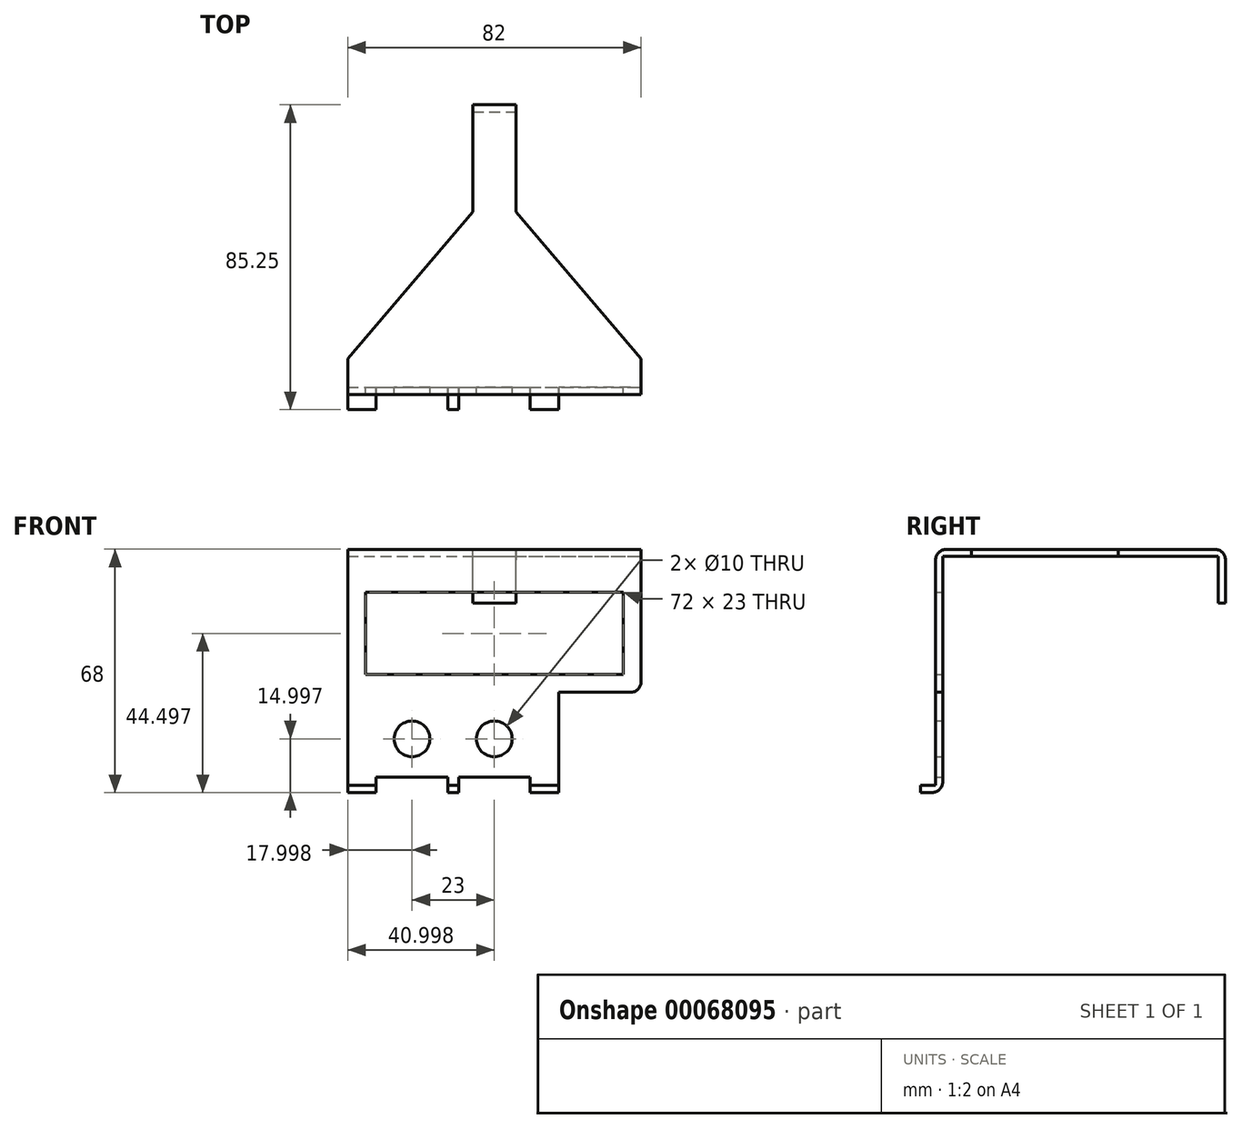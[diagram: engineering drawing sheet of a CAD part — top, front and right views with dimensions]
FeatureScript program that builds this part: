
annotation { "Feature Type Name" : "Feature", "Feature Type Description" : "" }
export const myFeature = defineFeature(function(context is Context, id is Id, definition is map)
    precondition{}
    {
        {
            var Q0;
            Q0=qCreatedBy(makeId("Front.planeOp"),FACE);
            var sketch = newSketch(context, id + "F0", { "sketchPlane" : qUnion([Q0])});
            skLineSegment(sketch, "E0.bottom", {"start": v(-52.13, 38.36) * mm, "end": v(29.87, 38.36) * mm});
            skLineSegment(sketch, "E0.top", {"start": v(-52.13, -29.64) * mm, "end": v(-44.13, -29.64) * mm});
            skLineSegment(sketch, "E0.left", {"start": v(-52.13, 38.36) * mm, "end": v(-52.13, -29.64) * mm});
            skLineSegment(sketch, "E0.right", {"start": v(29.87, 38.36) * mm, "end": v(29.87, 1.36) * mm});
            skLineSegment(sketch, "E1.bottom", {"start": v(-47.13, 26.36) * mm, "end": v(24.87, 26.36) * mm});
            skLineSegment(sketch, "E1.top", {"start": v(-47.13, 3.36) * mm, "end": v(24.87, 3.36) * mm});
            skLineSegment(sketch, "E1.left", {"start": v(-47.13, 26.36) * mm, "end": v(-47.13, 3.36) * mm});
            skLineSegment(sketch, "E1.right", {"start": v(24.87, 26.36) * mm, "end": v(24.87, 3.36) * mm});
            skLineSegment(sketch, "E2.top", {"start": v(26.87, -1.64) * mm, "end": v(6.87, -1.64) * mm});
            skLineSegment(sketch, "E2.right", {"start": v(6.87, -29.64) * mm, "end": v(6.87, -1.64) * mm});
            skLineSegment(sketch, "E3.top", {"start": v(-44.13, -25.4) * mm, "end": v(-24.13, -25.4) * mm});
            skLineSegment(sketch, "E3.left", {"start": v(-44.13, -29.64) * mm, "end": v(-44.13, -25.4) * mm});
            skLineSegment(sketch, "E3.right", {"start": v(-24.13, -29.64) * mm, "end": v(-24.13, -25.4) * mm});
            skLineSegment(sketch, "E4.top", {"start": v(-21.13, -25.4) * mm, "end": v(-1.13, -25.4) * mm});
            skLineSegment(sketch, "E4.left", {"start": v(-21.13, -29.64) * mm, "end": v(-21.13, -25.4) * mm});
            skLineSegment(sketch, "E4.right", {"start": v(-1.13, -29.64) * mm, "end": v(-1.13, -25.4) * mm});
            skLineSegment(sketch, "E5.trimOffspring", {"start": v(-24.13, -29.64) * mm, "end": v(-21.13, -29.64) * mm});
            skLineSegment(sketch, "E6.trimOffspring", {"start": v(-1.13, -29.64) * mm, "end": v(6.87, -29.64) * mm});
            skCircle(sketch, "E7", {"center": v(-11.13, -14.64) * mm, "radius": 5 * mm});
            skCircle(sketch, "E8", {"center": v(-34.13, -14.64) * mm, "radius": 5 * mm});
            skLineSegment(sketch, "E9.0", {"start": v(-52.13, -27.64) * mm, "end": v(-44.13, -27.64) * mm});
            skLineSegment(sketch, "E10.0", {"start": v(-24.13, -27.64) * mm, "end": v(-21.13, -27.64) * mm});
            skLineSegment(sketch, "E11.0", {"start": v(-1.13, -27.64) * mm, "end": v(6.87, -27.64) * mm});
            skPoint(sketch, "E12.visualSharp", {"position": v(29.87, -1.64) * mm});
            skArc(sketch, "E12.filletArc", {"start": v(26.87, -1.64) * mm, "mid": v(28.99, -0.76) * mm, "end": v(29.87, 1.36) * mm});
            skSolve(sketch);
        }
        {
            var Q0;
            {var subQ4=sQuery(id+"F0.wireOp",EDGE,"E0.bottom");Q0=makeQuery(id+"F0.imprint","IMPRINT",FACE,{"disambiguationData":[TD([[makeQuery(id+"F0.imprint","IMPRINT",EDGE,{"derivedFrom":subQ4}),-1.0]])]});}
            extrude(context, id + "F1", {"entities" : qUnion([Q0]), "depth" : 2 * mm});
        }
        {
            var Q0;
            {var subQ0=sQuery(id+"F0.wireOp",EDGE,"E0.top");Q0=makeQuery(id+"F0.imprint","IMPRINT",FACE,{"disambiguationData":[TD([[makeQuery(id+"F0.imprint","IMPRINT",EDGE,{"derivedFrom":subQ0}),1.0]])]});}
            var Q1;
            {var subQ0=sQuery(id+"F0.wireOp",EDGE,"E5.trimOffspring");Q1=makeQuery(id+"F0.imprint","IMPRINT",FACE,{"disambiguationData":[TD([[makeQuery(id+"F0.imprint","IMPRINT",EDGE,{"derivedFrom":subQ0}),1.0]])]});}
            var Q2;
            {var subQ0=sQuery(id+"F0.wireOp",EDGE,"E6.trimOffspring");Q2=makeQuery(id+"F0.imprint","IMPRINT",FACE,{"disambiguationData":[TD([[makeQuery(id+"F0.imprint","IMPRINT",EDGE,{"derivedFrom":subQ0}),1.0]])]});}
            extrude(context, id + "F2", {"entities" : qUnion([Q0, Q1, Q2]), "operationType" : NewBodyOperationType.ADD, "depth" : 6.25 * mm});
        }
        {
            var Q0;
            Q0=makeQuery(id+"F2.opExtrude","CAP_EDGE",EDGE,{"disambiguationData":[OSD([sQuery(id+"F0.wireOp",EDGE,"E0.top")])],"isStart":true});
            var Q1;
            Q1=makeQuery(id+"F2.opExtrude","CAP_EDGE",EDGE,{"disambiguationData":[OSD([sQuery(id+"F0.wireOp",EDGE,"E5.trimOffspring")])],"isStart":true});
            var Q2;
            Q2=makeQuery(id+"F2.opExtrude","CAP_EDGE",EDGE,{"disambiguationData":[OSD([sQuery(id+"F0.wireOp",EDGE,"E6.trimOffspring")])],"isStart":true});
            fillet(context, id + "F3", {"entities" : qUnion([Q0, Q1, Q2]), "radius" : 3 * mm, "tangentPropagation" : true, "allowEdgeOverflow" : false});
        }
        {
            var Q0;
            Q0=makeQuery(id+"F1.opExtrude","SWEPT_FACE",FACE,{"disambiguationData":[OSD([sQuery(id+"F0.wireOp",EDGE,"E0.bottom")])]});
            var sketch = newSketch(context, id + "F4", { "sketchPlane" : qUnion([Q0])});
            skPoint(sketch, "E13", {"position": v(-52.13, -2) * mm});
            skPoint(sketch, "E14", {"position": v(29.87, -2) * mm});
            skLineSegment(sketch, "E15", {"start": v(-52.13, -2) * mm, "end": v(-52.13, 8) * mm});
            skLineSegment(sketch, "E16", {"start": v(-52.13, 8) * mm, "end": v(-17.13, 49) * mm});
            skLineSegment(sketch, "E17", {"start": v(-17.13, 49) * mm, "end": v(-17.13, 79) * mm});
            skLineSegment(sketch, "E18", {"start": v(-17.13, 79) * mm, "end": v(-5.13, 79) * mm});
            skLineSegment(sketch, "E19", {"start": v(-5.13, 79) * mm, "end": v(-5.13, 49) * mm});
            skLineSegment(sketch, "E20", {"start": v(-5.13, 49) * mm, "end": v(29.87, 8) * mm});
            skLineSegment(sketch, "E21", {"start": v(29.87, -2) * mm, "end": v(29.87, 8) * mm});
            skLineSegment(sketch, "E22.0", {"start": v(-17.13, 77) * mm, "end": v(-5.13, 77) * mm});
            skSolve(sketch);
        }
        {
            var Q0;
            {var subQ4=sQuery(id+"F4.wireOp",EDGE,"E16");Q0=makeQuery(id+"F4.imprint","IMPRINT",FACE,{"disambiguationData":[TD([[makeQuery(id+"F4.imprint","IMPRINT",EDGE,{"derivedFrom":subQ4}),-1.0]])]});}
            extrude(context, id + "F5", {"entities" : qUnion([Q0]), "operationType" : NewBodyOperationType.ADD, "oppositeDirection" : true, "depth" : 2 * mm});
        }
        {
            var Q0;
            {var subQ0=sQuery(id+"F4.wireOp",EDGE,"E18");Q0=makeQuery(id+"F4.imprint","IMPRINT",FACE,{"disambiguationData":[TD([[makeQuery(id+"F4.imprint","IMPRINT",EDGE,{"derivedFrom":subQ0}),-1.0]])]});}
            extrude(context, id + "F6", {"entities" : qUnion([Q0]), "operationType" : NewBodyOperationType.ADD, "oppositeDirection" : true, "depth" : 15 * mm});
        }
        {
            var Q0;
            Q0=makeQuery(id+"F6.opExtrude","CAP_EDGE",EDGE,{"disambiguationData":[OSD([sQuery(id+"F4.wireOp",EDGE,"E18")])],"isStart":true});
            var Q1;
            Q1=makeQuery(id+"F1.opExtrude","CAP_EDGE",EDGE,{"disambiguationData":[OSD([sQuery(id+"F0.wireOp",EDGE,"E0.bottom")])],"isStart":false});
            fillet(context, id + "F7", {"entities" : qUnion([Q0, Q1]), "radius" : 3 * mm, "tangentPropagation" : true, "allowEdgeOverflow" : false});
        }
    });
